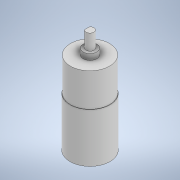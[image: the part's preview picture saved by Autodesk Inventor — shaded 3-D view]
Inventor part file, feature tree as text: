
AUTODESK INVENTOR PART (.ipt)
format: ipt  version: 2022 (Build 260153000, 153)  size: 124,928 bytes
history: native  units: mm
features: extrude x5, sketch x5, projected_geometry x1
ambient origin geometry x8: Origin, YZ Plane, XZ Plane, XY Plane, X Axis, Y Axis, Z Axis, Center Point
bodies: Solid1 (feature_tree)
feature tree (11):
  extrude  "Extrusion1"  Depth=25.1mm TaperAngle=0.0deg
  extrude  "Extrusion2"  Depth=17.0mm TaperAngle=0.0deg
  extrude  "Extrusion3"  Depth=3.0mm TaperAngle=0.0deg
  extrude  "Extrusion4"  Depth=8.0mm TaperAngle=0.0deg
  extrude  "Extrusion5"  Depth=7.0mm TaperAngle=0.0deg
  sketch  "Sketch1"  dims[d0=20.4mm d1=25.1mm d2=0.0mm]
  sketch  "Sketch2"  dims[d3=20.0mm d4=17.0mm d5=0.0mm]
  sketch  "Sketch3"  dims[d6=7.0mm d7=3.0mm d8=0.0mm]
  sketch  "Sketch4"  dims[d9=4.0mm d10=8.0mm d11=0.0mm]
  sketch  "Sketch5"  dims[d12=0.5mm d13=7.0mm d14=0.0mm]
  projected_geometry  "Projected Loop1"
